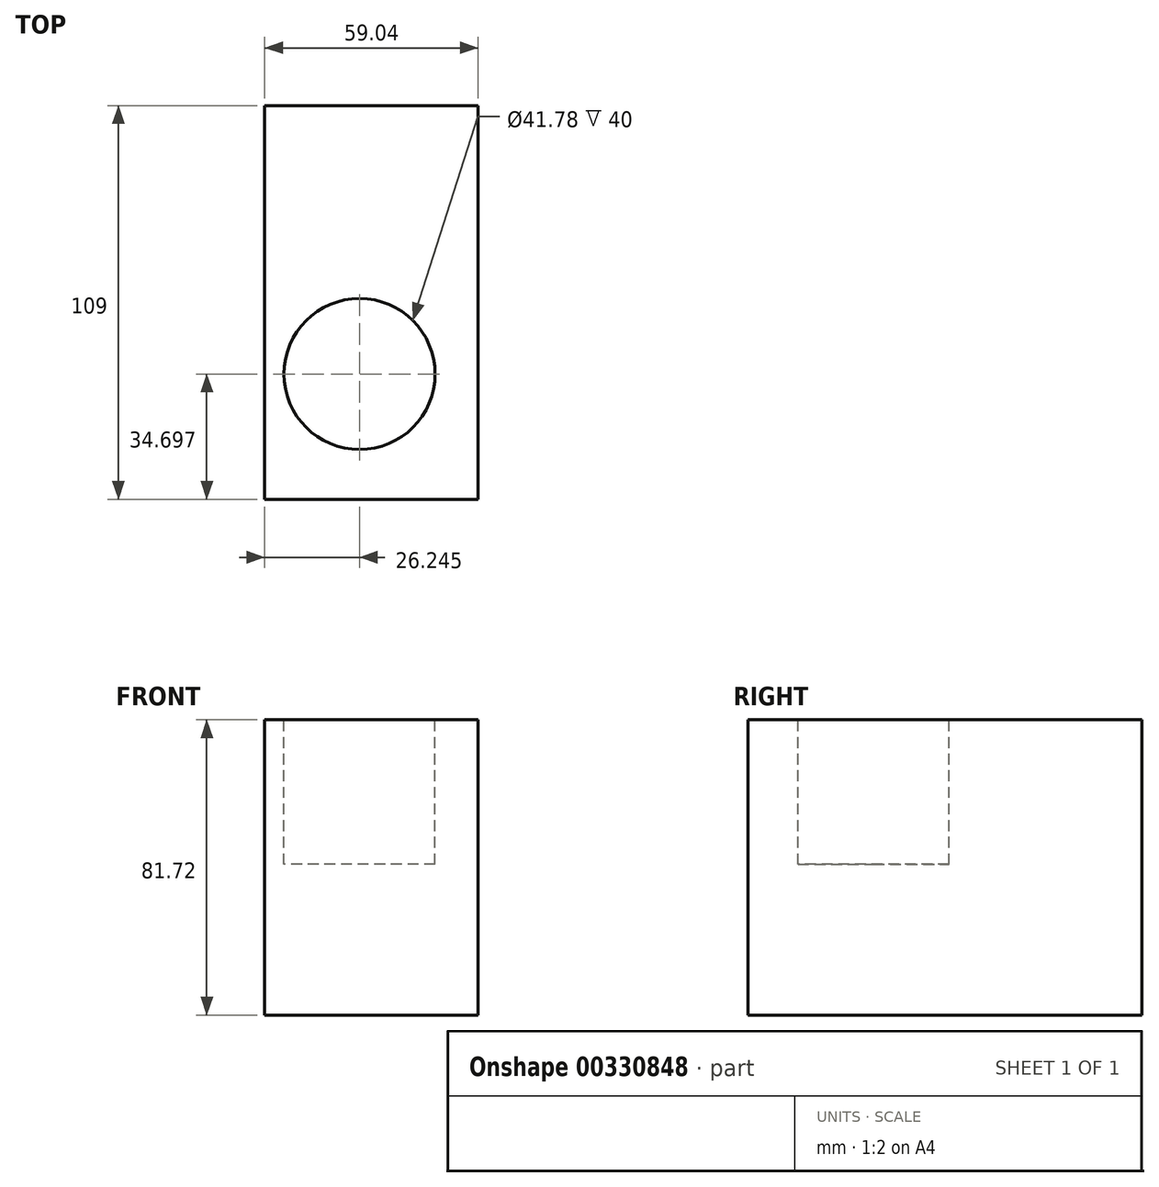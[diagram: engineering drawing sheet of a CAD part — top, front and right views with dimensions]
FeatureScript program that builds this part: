
annotation { "Feature Type Name" : "Feature", "Feature Type Description" : "" }
export const myFeature = defineFeature(function(context is Context, id is Id, definition is map)
    precondition{}
    {
        {
            var Q0;
            Q0=qCreatedBy(makeId("Front.planeOp"),FACE);
            var sketch = newSketch(context, id + "F0", { "sketchPlane" : qUnion([Q0])});
            skLineSegment(sketch, "E0.bottom", {"start": v(-99.84, -46.4) * mm, "end": v(-40.8, -46.4) * mm});
            skLineSegment(sketch, "E0.top", {"start": v(-99.84, 35.32) * mm, "end": v(-40.8, 35.32) * mm});
            skLineSegment(sketch, "E0.left", {"start": v(-99.84, -46.4) * mm, "end": v(-99.84, 35.32) * mm});
            skLineSegment(sketch, "E0.right", {"start": v(-40.8, -46.4) * mm, "end": v(-40.8, 35.32) * mm});
            skSolve(sketch);
        }
        {
            var Q0;
            Q0=makeQuery(id+"F0.imprint","IMPRINT",FACE,{"disambiguationData":[TD([[makeQuery(id+"F0.imprint","IMPRINT",EDGE,{"derivedFrom":sQuery(id+"F0.wireOp",EDGE,"E0.bottom")}),1.0]])]});
            extrude(context, id + "F1", {"entities" : qUnion([Q0]), "depth" : 109 * mm});
        }
        {
            var Q0;
            Q0=makeQuery(id+"F1.opExtrude","SWEPT_FACE",FACE,{"disambiguationData":[OSD([sQuery(id+"F0.wireOp",EDGE,"E0.top")])]});
            var sketch = newSketch(context, id + "F2", { "sketchPlane" : qUnion([Q0])});
            skCircle(sketch, "E1", {"center": v(-73.6, -74.3) * mm, "radius": 20.9 * mm});
            skSolve(sketch);
        }
        {
            var Q0;
            Q0=makeQuery(id+"F2.imprint","IMPRINT",FACE,{"disambiguationData":[TD([[makeQuery(id+"F2.imprint","IMPRINT",EDGE,{"derivedFrom":sQuery(id+"F2.wireOp",EDGE,"E1")}),1.0]])]});
            extrude(context, id + "F3", {"entities" : qUnion([Q0]), "operationType" : NewBodyOperationType.REMOVE, "oppositeDirection" : true, "depth" : 40 * mm});
        }
    });
